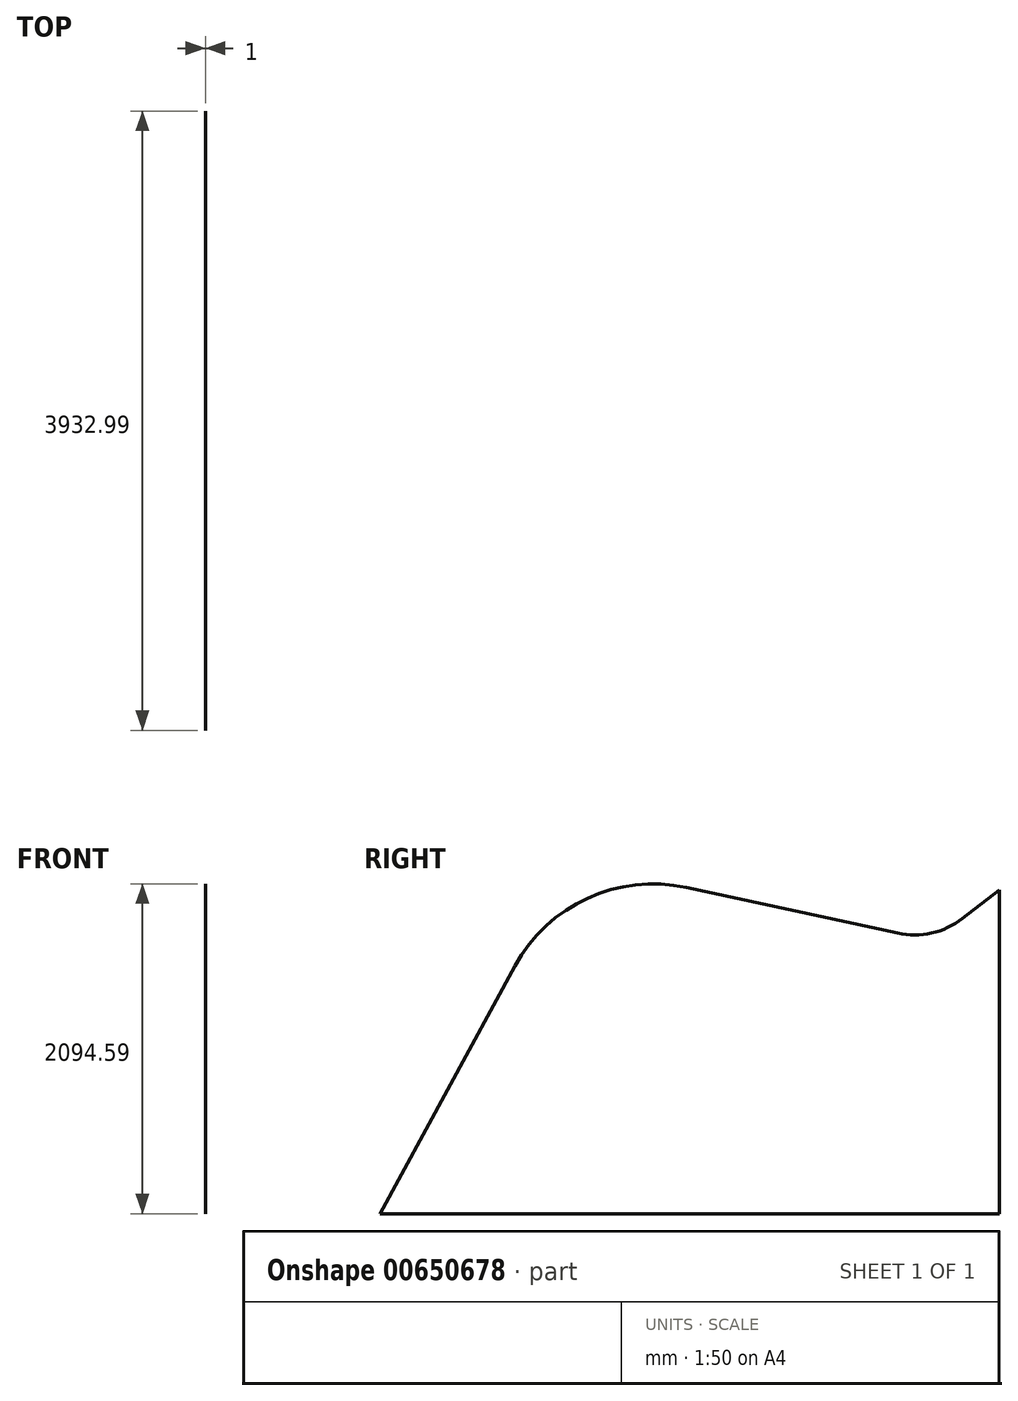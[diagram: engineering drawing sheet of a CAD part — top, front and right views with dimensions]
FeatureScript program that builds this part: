
annotation { "Feature Type Name" : "Feature", "Feature Type Description" : "" }
export const myFeature = defineFeature(function(context is Context, id is Id, definition is map)
    precondition{}
    {
        {
            var Q0;
            Q0=qCreatedBy(makeId("Right.planeOp"),FACE);
            var sketch = newSketch(context, id + "F0", { "sketchPlane" : qUnion([Q0])});
            skLineSegment(sketch, "E0.bottom", {"start": v(-4475.06, -1796.92) * mm, "end": v(2424.94, -1796.92) * mm});
            skLineSegment(sketch, "E0.top", {"start": v(-4475.06, 1503.08) * mm, "end": v(2424.94, 1503.08) * mm});
            skLineSegment(sketch, "E0.left", {"start": v(-4475.06, -1796.92) * mm, "end": v(-4475.06, 1503.08) * mm});
            skLineSegment(sketch, "E0.right", {"start": v(2424.94, -1796.92) * mm, "end": v(2424.94, 1503.08) * mm});
            skLineSegment(sketch, "E1", {"start": v(-4475.06, -1796.92) * mm, "end": v(-3619.55, -224.43) * mm});
            skLineSegment(sketch, "E2", {"start": v(974.94, -1796.92) * mm, "end": v(974.94, 277.38) * mm});
            skLineSegment(sketch, "E3", {"start": v(974.94, 277.38) * mm, "end": v(-25.06, 277.38) * mm});
            skLineSegment(sketch, "E4", {"start": v(-25.06, 277.38) * mm, "end": v(-25.06, -1796.92) * mm});
            skLineSegment(sketch, "E5", {"start": v(-2529.68, 275.06) * mm, "end": v(-1187.85, -15.25) * mm});
            skLineSegment(sketch, "E6", {"start": v(-777.06, 77.3) * mm, "end": v(76.44, 734.55) * mm});
            skLineSegment(sketch, "E7", {"start": v(1558.4, 432.06) * mm, "end": v(1831.71, -54.42) * mm});
            skLineSegment(sketch, "E8", {"start": v(1982.26, -186.18) * mm, "end": v(2424.94, -362.49) * mm});
            skPoint(sketch, "E9.visualSharp", {"position": v(-3261.65, 433.42) * mm});
            skArc(sketch, "E9.filletArc", {"start": v(-2529.68, 275.06) * mm, "mid": v(-3157.76, 206.75) * mm, "end": v(-3619.55, -224.43) * mm});
            skPoint(sketch, "E10", {"position": v(2424.94, -146.92) * mm});
            skPoint(sketch, "E11.visualSharp", {"position": v(-960.97, -64.34) * mm});
            skArc(sketch, "E11.filletArc", {"start": v(-1187.85, -15.25) * mm, "mid": v(-972.24, -14.33) * mm, "end": v(-777.06, 77.3) * mm});
            skPoint(sketch, "E12.visualSharp", {"position": v(992.24, 1439.79) * mm});
            skArc(sketch, "E12.filletArc", {"start": v(1558.4, 432.06) * mm, "mid": v(886.57, 922.05) * mm, "end": v(76.44, 734.55) * mm});
            skPoint(sketch, "E13.visualSharp", {"position": v(1883.69, -146.92) * mm});
            skArc(sketch, "E13.filletArc", {"start": v(1831.71, -54.42) * mm, "mid": v(1895.68, -133.22) * mm, "end": v(1982.26, -186.18) * mm});
            skSolve(sketch);
        }
        {
            var Q0;
            {var subQ2=sQuery(id+"F0.wireOp",EDGE,"E1");Q0=makeQuery(id+"F0.imprint","IMPRINT",FACE,{"disambiguationData":[TD([[makeQuery(id+"F0.imprint","IMPRINT",EDGE,{"derivedFrom":subQ2}),-1.0]])]});}
            extrude(context, id + "F1", {"entities" : qUnion([Q0]), "depth" : 1 * mm, "offsetDistance" : 25 * mm});
        }
        {
            var Q0;
            Q0=makeQuery(id+"F1.opExtrude","CAP_FACE",FACE,{"disambiguationData":[OSD([sQuery(id+"F0.wireOp",EDGE,"E0.bottom"),sQuery(id+"F0.wireOp",EDGE,"E0.right"),sQuery(id+"F0.wireOp",EDGE,"E1"),sQuery(id+"F0.wireOp",EDGE,"E2"),sQuery(id+"F0.wireOp",EDGE,"E3"),sQuery(id+"F0.wireOp",EDGE,"E4"),sQuery(id+"F0.wireOp",EDGE,"E5"),sQuery(id+"F0.wireOp",EDGE,"E6"),sQuery(id+"F0.wireOp",EDGE,"E7"),sQuery(id+"F0.wireOp",EDGE,"E8"),sQuery(id+"F0.wireOp",EDGE,"E9.filletArc"),sQuery(id+"F0.wireOp",EDGE,"E11.filletArc"),sQuery(id+"F0.wireOp",EDGE,"E12.filletArc"),sQuery(id+"F0.wireOp",EDGE,"E13.filletArc")])],"isStart":false});
            var sketch = newSketch(context, id + "F2", { "sketchPlane" : qUnion([Q0])});
            skLineSegment(sketch, "E14.bottom", {"start": v(-542.07, 1072.96) * mm, "end": v(2683.42, 1072.96) * mm});
            skLineSegment(sketch, "E14.top", {"start": v(-542.07, -1870.9) * mm, "end": v(2683.42, -1870.9) * mm});
            skLineSegment(sketch, "E14.left", {"start": v(-542.07, 1072.96) * mm, "end": v(-542.07, -1870.9) * mm});
            skLineSegment(sketch, "E14.right", {"start": v(2683.42, 1072.96) * mm, "end": v(2683.42, -1870.9) * mm});
            skSolve(sketch);
        }
        {
            var Q0;
            Q0 = qSketchRegion(id + "F2", true);
            extrude(context, id + "F3", {"entities" : qUnion([Q0]), "operationType" : NewBodyOperationType.REMOVE, "oppositeDirection" : true, "depth" : 1000 * mm, "offsetDistance" : 25 * mm});
        }
    });
